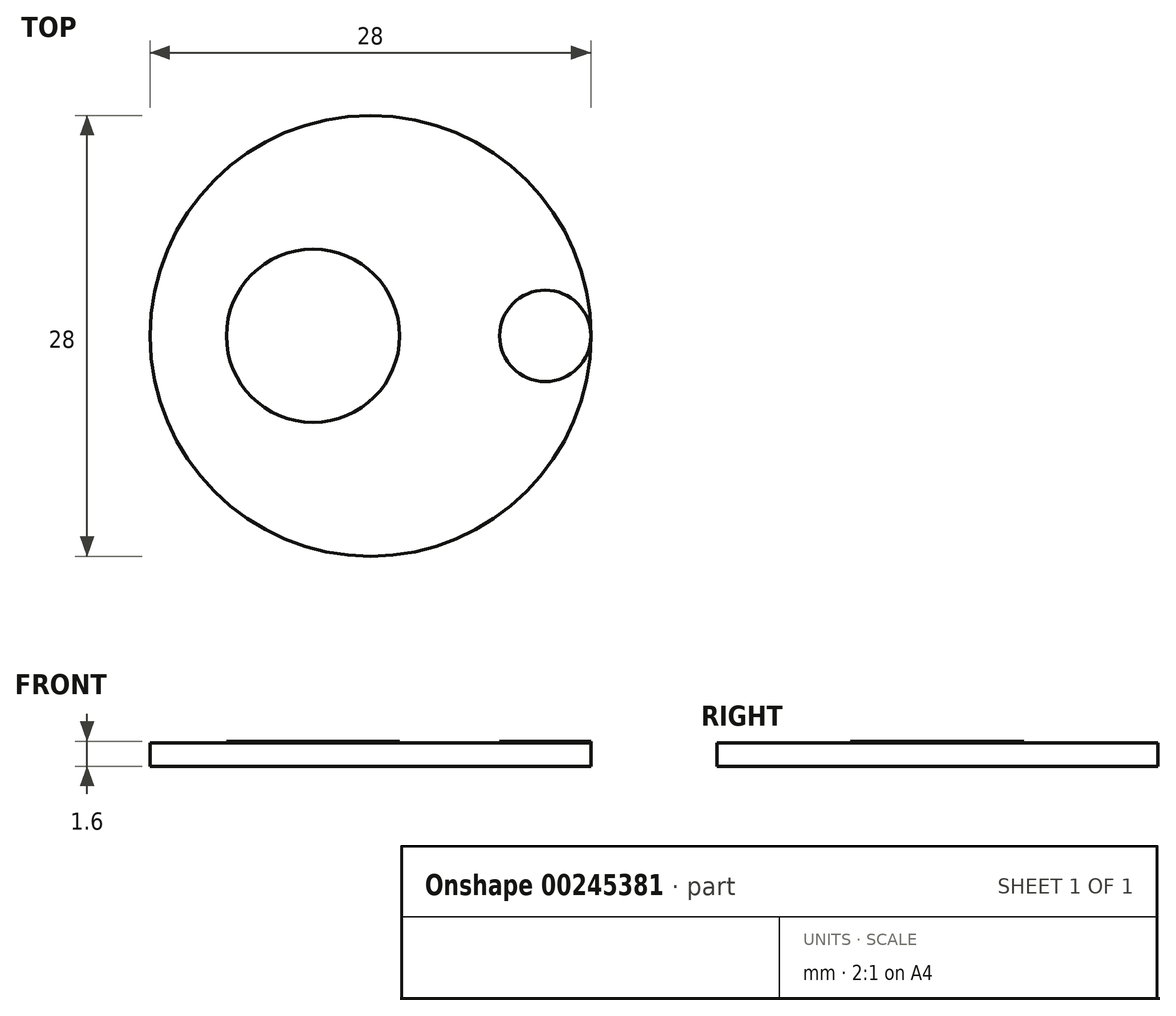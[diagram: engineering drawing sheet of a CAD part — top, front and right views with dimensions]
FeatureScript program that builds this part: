
annotation { "Feature Type Name" : "Feature", "Feature Type Description" : "" }
export const myFeature = defineFeature(function(context is Context, id is Id, definition is map)
    precondition{}
    {
        {
            var Q0;
            Q0=qCreatedBy(makeId("Top.planeOp"),FACE);
            var sketch = newSketch(context, id + "F0", { "sketchPlane" : qUnion([Q0])});
            skCircle(sketch, "E0", {"center": v(0, 0) * mm, "radius": 14 * mm});
            skCircle(sketch, "E1", {"center": v(-3.65, 0) * mm, "radius": 10.35 * mm, "construction": true});
            skCircle(sketch, "E2", {"center": v(11.1, 0) * mm, "radius": 2.9 * mm, "construction": true});
            skSolve(sketch);
        }
        {
            var Q0;
            Q0 = qSketchRegion(id + "F0", true);
            extrude(context, id + "F1", {"entities" : qUnion([Q0]), "depth" : 1.5 * mm});
        }
        {
            var Q0;
            Q0=makeQuery(id+"F1.opExtrude","CAP_FACE",FACE,{"disambiguationData":[OSD([sQuery(id+"F0.wireOp",EDGE,"E0")])],"isStart":false});
            var sketch = newSketch(context, id + "F2", { "sketchPlane" : qUnion([Q0])});
            skCircle(sketch, "E3", {"center": v(-3.65, 0) * mm, "radius": 5.5 * mm});
            skCircle(sketch, "E4", {"center": v(11.1, 0) * mm, "radius": 2.9 * mm});
            skSolve(sketch);
        }
        {
            var Q0;
            Q0 = qSketchRegion(id + "F2", true);
            extrude(context, id + "F3", {"entities" : qUnion([Q0]), "operationType" : NewBodyOperationType.ADD, "depth" : 0.1 * mm});
        }
    });
